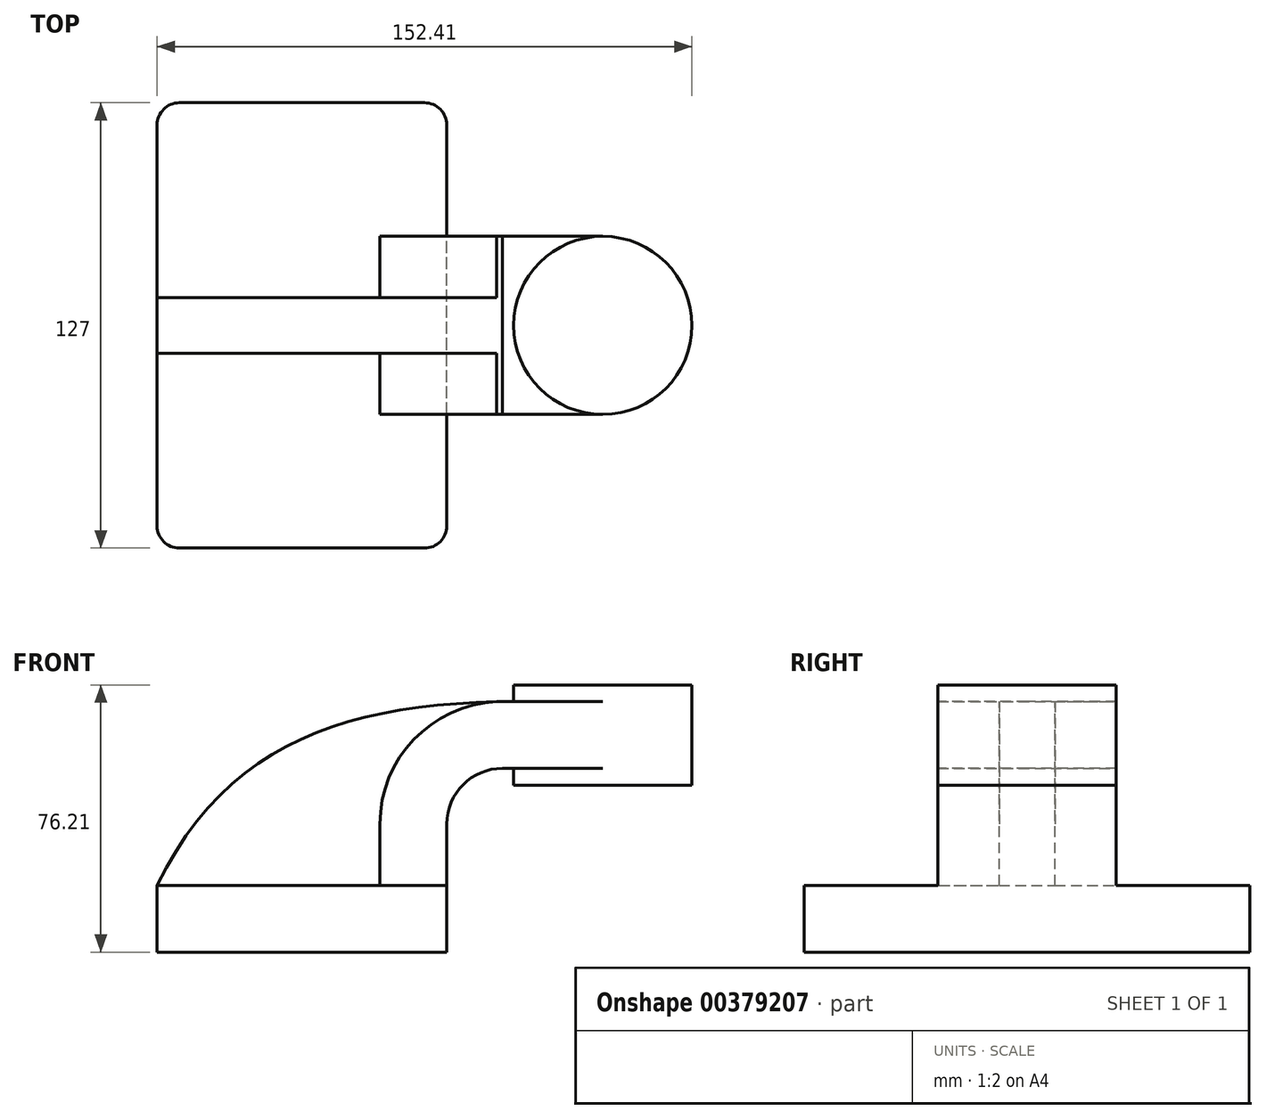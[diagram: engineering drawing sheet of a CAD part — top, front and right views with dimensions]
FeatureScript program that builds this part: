
annotation { "Feature Type Name" : "Feature", "Feature Type Description" : "" }
export const myFeature = defineFeature(function(context is Context, id is Id, definition is map)
    precondition{}
    {
        {
            var Q0;
            Q0=qCreatedBy(makeId("Front.planeOp"),FACE);
            var sketch = newSketch(context, id + "F0", { "sketchPlane" : qUnion([Q0])});
            skLineSegment(sketch, "E0.bottom", {"start": v(41.28, -9.52) * mm, "end": v(-41.27, -9.53) * mm});
            skLineSegment(sketch, "E0.top", {"start": v(41.27, 9.53) * mm, "end": v(-41.28, 9.53) * mm});
            skLineSegment(sketch, "E0.left", {"start": v(41.28, -9.52) * mm, "end": v(41.28, 9.53) * mm});
            skLineSegment(sketch, "E0.right", {"start": v(-41.27, -9.53) * mm, "end": v(-41.28, 9.53) * mm});
            skPoint(sketch, "E0.middle", {"position": v(0, 0) * mm});
            skLineSegment(sketch, "E1.bottom", {"start": v(111.12, 38.1) * mm, "end": v(60.32, 38.1) * mm});
            skLineSegment(sketch, "E1.top", {"start": v(111.12, 66.68) * mm, "end": v(60.32, 66.68) * mm});
            skLineSegment(sketch, "E1.left", {"start": v(111.12, 38.1) * mm, "end": v(111.12, 66.68) * mm});
            skLineSegment(sketch, "E1.right", {"start": v(60.32, 38.1) * mm, "end": v(60.32, 66.68) * mm});
            skPoint(sketch, "E1.middle", {"position": v(85.72, 52.39) * mm});
            skLineSegment(sketch, "E2", {"start": v(41.27, 9.53) * mm, "end": v(41.27, 27) * mm});
            skArc(sketch, "E3", {"start": v(41.27, 27) * mm, "mid": v(45.92, 38.23) * mm, "end": v(57.15, 42.88) * mm});
            skLineSegment(sketch, "E4", {"start": v(57.15, 42.88) * mm, "end": v(85.72, 42.88) * mm});
            skPoint(sketch, "E4.endSnap0", {"position": v(85.72, 38.1) * mm});
            skLineSegment(sketch, "E5.0", {"start": v(57.15, 61.93) * mm, "end": v(85.72, 61.93) * mm});
            skArc(sketch, "E5.1", {"start": v(22.23, 27) * mm, "mid": v(32.45, 51.7) * mm, "end": v(57.15, 61.93) * mm});
            skLineSegment(sketch, "E5.2", {"start": v(22.22, 9.53) * mm, "end": v(22.22, 27) * mm});
            skLineSegment(sketch, "E6", {"start": v(85.72, 38.1) * mm, "end": v(85.72, 66.68) * mm});
            skFitSpline(sketch, "E7", {"points": [v(-41.28, 9.52) * mm, v(57.15, 61.93) * mm], "startDerivative": vector(59.04, 120.69) * mm, "endDerivative": vector(137.2, 2.95) * mm});
            skSolve(sketch);
        }
        {
            var Q0;
            Q0=makeQuery(id+"F0.imprint","IMPRINT",FACE,{"disambiguationData":[TD([[makeQuery(id+"F0.imprint","IMPRINT",EDGE,{"derivedFrom":sQuery(id+"F0.wireOp",EDGE,"E0.bottom")}),-1.0]])]});
            extrude(context, id + "F1", {"entities" : qUnion([Q0]), "endBound" : BoundingType.SYMMETRIC, "depth" : 127 * mm});
        }
        {
            var Q0;
            {var subQ1=sQuery(id+"F0.wireOp",EDGE,"E2");Q0=makeQuery(id+"F0.imprint","IMPRINT",FACE,{"disambiguationData":[TD([[makeQuery(id+"F0.imprint","IMPRINT",EDGE,{"derivedFrom":subQ1}),1.0]])]});}
            var Q1;
            {var subQ0=sQuery(id+"F0.wireOp",EDGE,"E4");var subQ1=sQuery(id+"F0.wireOp",EDGE,"E1.right");var subQ2=makeQuery(id+"F0.imprint","INTERSECT",VERTEX,{"derivedFrom":[subQ1,subQ0]});Q1=makeQuery(id+"F0.imprint","IMPRINT",FACE,{"disambiguationData":[TD([[makeQuery(id+"F0.imprint","IMPRINT",EDGE,{"disambiguationData":[TD([[subQ2,-1.0]])],"derivedFrom":subQ1}),-1.0]])]});}
            extrude(context, id + "F2", {"entities" : qUnion([Q0, Q1]), "operationType" : NewBodyOperationType.ADD, "endBound" : BoundingType.SYMMETRIC, "depth" : 50.8 * mm});
        }
        {
            var Q0;
            {var subQ3=sQuery(id+"F0.wireOp",EDGE,"E5.2");Q0=makeQuery(id+"F0.imprint","IMPRINT",FACE,{"disambiguationData":[TD([[makeQuery(id+"F0.imprint","IMPRINT",EDGE,{"derivedFrom":subQ3}),1.0]])]});}
            extrude(context, id + "F3", {"entities" : qUnion([Q0]), "operationType" : NewBodyOperationType.ADD, "endBound" : BoundingType.SYMMETRIC, "depth" : 15.88 * mm});
        }
        {
            var Q0;
            {var subQ0=sQuery(id+"F0.wireOp",EDGE,"E1.left");Q0=makeQuery(id+"F0.imprint","IMPRINT",FACE,{"disambiguationData":[TD([[makeQuery(id+"F0.imprint","IMPRINT",EDGE,{"derivedFrom":subQ0}),1.0]])]});}
            var Q1;
            Q1=sQuery(id+"F0.wireOp",EDGE,"E6");
            revolve(context, id + "F4", {"operationType" : NewBodyOperationType.ADD, "entities" : qUnion([Q0]), "axis" : qUnion([Q1]), "revolveType" : RevolveType.FULL});
        }
        {
            var Q0;
            Q0=makeQuery(id+"F1.opExtrude","CAP_EDGE",EDGE,{"disambiguationData":[OSD([sQuery(id+"F0.wireOp",EDGE,"E0.right")])],"isStart":false});
            var Q1;
            Q1=makeQuery(id+"F1.opExtrude","CAP_EDGE",EDGE,{"disambiguationData":[OSD([sQuery(id+"F0.wireOp",EDGE,"E0.left")])],"isStart":false});
            var Q2;
            Q2=makeQuery(id+"F1.opExtrude","CAP_EDGE",EDGE,{"disambiguationData":[OSD([sQuery(id+"F0.wireOp",EDGE,"E0.left")])],"isStart":true});
            var Q3;
            Q3=makeQuery(id+"F1.opExtrude","CAP_EDGE",EDGE,{"disambiguationData":[OSD([sQuery(id+"F0.wireOp",EDGE,"E0.right")])],"isStart":true});
            fillet(context, id + "F5", {"entities" : qUnion([Q0, Q1, Q2, Q3]), "radius" : 6.35 * mm, "tangentPropagation" : true, "allowEdgeOverflow" : false});
        }
    });
